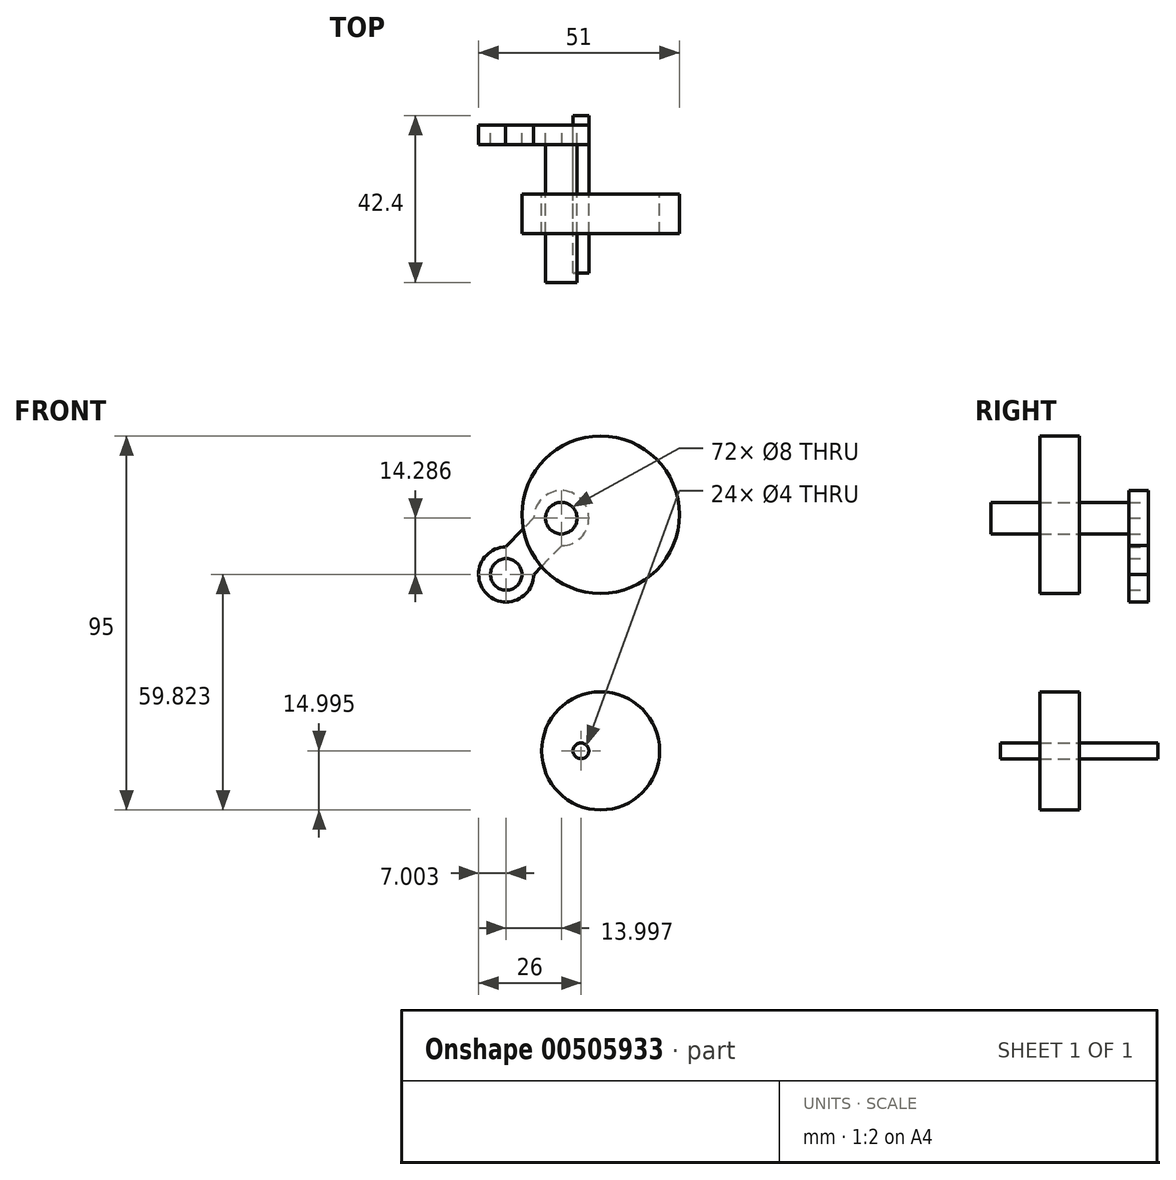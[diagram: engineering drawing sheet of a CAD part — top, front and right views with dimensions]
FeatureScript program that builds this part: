
annotation { "Feature Type Name" : "Feature", "Feature Type Description" : "" }
export const myFeature = defineFeature(function(context is Context, id is Id, definition is map)
    precondition{}
    {
        {
            var Q0;
            Q0=qCreatedBy(makeId("Front.planeOp"),FACE);
            var sketch = newSketch(context, id + "F0", { "sketchPlane" : qUnion([Q0])});
            skCircle(sketch, "E0", {"center": v(0, 32.36) * mm, "radius": 20 * mm});
            skCircle(sketch, "E1", {"center": v(0, -27.64) * mm, "radius": 15 * mm});
            skLineSegment(sketch, "E2", {"start": v(-10, 31.47) * mm, "end": v(-5, -27.64) * mm});
            skSolve(sketch);
        }
        {
            var Q0;
            Q0 = qSketchRegion(id + "F0", true);
            extrude(context, id + "F1", {"entities" : qUnion([Q0]), "depth" : 10 * mm});
        }
        {
            var Q0;
            Q0=makeQuery(id+"F0.imprint","IMPRINT",FACE,{"disambiguationData":[TD([[makeQuery(id+"F0.imprint","IMPRINT",EDGE,{"derivedFrom":sQuery(id+"F0.wireOp",EDGE,"E1")}),1.0]])]});
            var sketch = newSketch(context, id + "F2", { "sketchPlane" : qUnion([Q0])});
            skLineSegment(sketch, "E3.0", {"start": v(-10, 31.47) * mm, "end": v(-9.66, 27.48) * mm});
            skCircle(sketch, "E4", {"center": v(-5, -27.64) * mm, "radius": 2 * mm});
            skCircle(sketch, "E5", {"center": v(-10, 31.47) * mm, "radius": 4 * mm});
            skLineSegment(sketch, "E6", {"start": v(-3, -27.64) * mm, "end": v(-3.01, -27.44) * mm});
            skLineSegment(sketch, "E7.trimOffspring", {"start": v(-5.17, -25.65) * mm, "end": v(-5, -27.64) * mm});
            skPoint(sketch, "E8.start.orphan", {"position": v(-7, -27.64) * mm});
            skSolve(sketch);
        }
        {
            var Q0;
            {var subQ0=sQuery(id+"F2.wireOp",EDGE,"E6");var subQ5=makeQuery(id+"F2.imprint","IMPRINT",EDGE,{"derivedFrom":subQ0});var subQ6=sQuery(id+"F2.wireOp",EDGE,"E5");Q0=qUnion([makeQuery(id+"F2.imprint","IMPRINT",FACE,{"disambiguationData":[TD([[makeQuery(id+"F2.imprint","IMPRINT",EDGE,{"disambiguationData":[TD([[makeQuery(id+"F2.imprint","IMPRINT",VERTEX,{"derivedFrom":subQ6}),-1.0]])],"derivedFrom":subQ6}),1.0]])]}),makeQuery(id+"F2.imprint","IMPRINT",FACE,{"disambiguationData":[TD([[subQ5,-1.0]])]}),makeQuery(id+"F2.imprint","IMPRINT",FACE,{"disambiguationData":[TD([[subQ5,1.0]])]})]);}
            extrude(context, id + "F3", {"entities" : qUnion([Q0]), "operationType" : NewBodyOperationType.REMOVE, "depth" : 25 * mm});
        }
        {
            var Q0;
            Q0=makeQuery(id+"F0.imprint","IMPRINT",FACE,{"disambiguationData":[TD([[makeQuery(id+"F0.imprint","IMPRINT",EDGE,{"derivedFrom":sQuery(id+"F0.wireOp",EDGE,"E0")}),1.0]])]});
            var sketch = newSketch(context, id + "F4", { "sketchPlane" : qUnion([Q0])});
            skCircle(sketch, "E9.0", {"center": v(-10, 31.47) * mm, "radius": 4 * mm});
            skCircle(sketch, "E10.0", {"center": v(-5, -27.64) * mm, "radius": 2 * mm});
            skSolve(sketch);
        }
        {
            var Q0;
            Q0 = qSketchRegion(id + "F4", true);
            extrude(context, id + "F5", {"entities" : qUnion([Q0]), "depth" : 40 * mm, "offsetDistance" : 25 * mm, "symmetric" : true});
        }
        {
            var Q0;
            Q0=makeQuery(id+"F5.opExtrude","SWEPT_BODY",BODY,{"disambiguationData":[OSD([sQuery(id+"F4.wireOp",EDGE,"E9.0")])]});
            transform(context, id + "F6", {"entities" : qUnion([Q0]), "transformType" : TransformType.TRANSLATION_3D, "dx" : 0 * mm, "dy" : -2.4 * mm, "dz" : 0 * mm, "makeCopy" : false});
        }
        {
            var Q0;
            Q0=makeQuery(id+"F5.opExtrude","CAP_FACE",FACE,{"disambiguationData":[OSD([sQuery(id+"F4.wireOp",EDGE,"E9.0")])],"isStart":true});
            var sketch = newSketch(context, id + "F7", { "sketchPlane" : qUnion([Q0])});
            skCircle(sketch, "E11", {"center": v(10, 31.47) * mm, "radius": 7 * mm});
            skCircle(sketch, "E12.0", {"center": v(10, 31.47) * mm, "radius": 4 * mm});
            skLineSegment(sketch, "E13", {"start": v(9.86, 24.47) * mm, "end": v(17, 17.18) * mm});
            skLineSegment(sketch, "E14", {"start": v(17, 31.47) * mm, "end": v(24.14, 24.18) * mm});
            skLineSegment(sketch, "E15", {"start": v(10, 31.47) * mm, "end": v(24, 17.18) * mm});
            skCircle(sketch, "E16", {"center": v(24, 17.18) * mm, "radius": 7 * mm});
            skCircle(sketch, "E17", {"center": v(24, 17.18) * mm, "radius": 4 * mm});
            skSolve(sketch);
        }
        {
            var Q0;
            Q0 = qSketchRegion(id + "F7", true);
            extrude(context, id + "F8", {"entities" : qUnion([Q0]), "oppositeDirection" : true, "depth" : 5 * mm, "offsetDistance" : 25 * mm});
        }
    });
